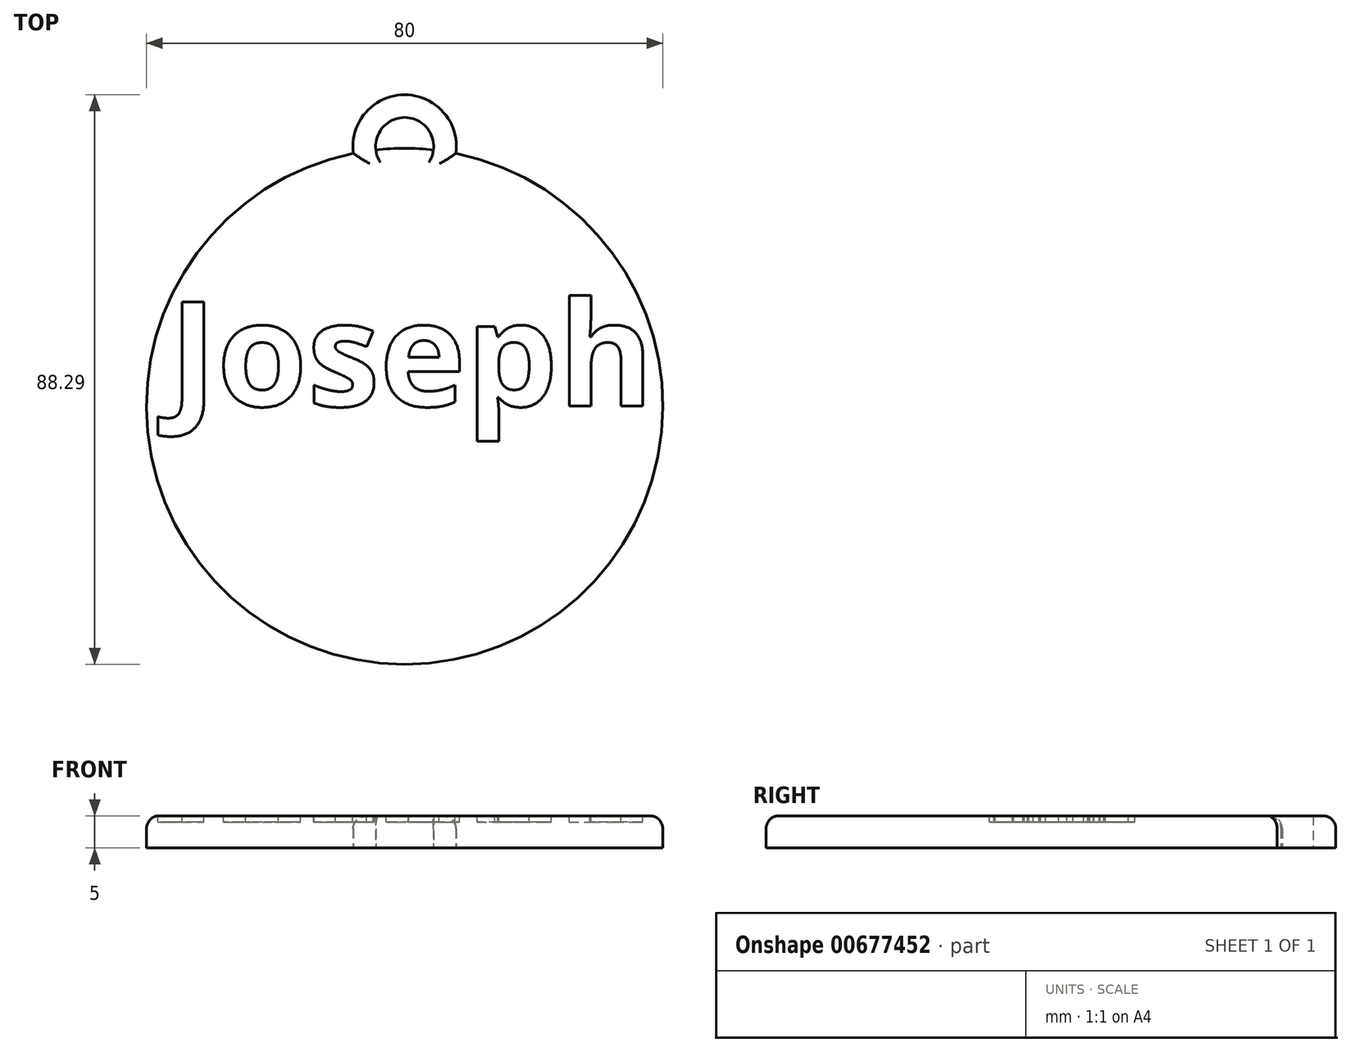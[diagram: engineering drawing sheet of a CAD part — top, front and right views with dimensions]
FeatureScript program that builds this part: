
annotation { "Feature Type Name" : "Feature", "Feature Type Description" : "" }
export const myFeature = defineFeature(function(context is Context, id is Id, definition is map)
    precondition{}
    {
        {
            var Q0;
            Q0=qCreatedBy(makeId("Top.planeOp"),FACE);
            var sketch = newSketch(context, id + "F0", { "sketchPlane" : qUnion([Q0])});
            skCircle(sketch, "E0", {"center": v(0, 0) * mm, "radius": 40 * mm});
            skSolve(sketch);
        }
        {
            var Q0;
            Q0 = qSketchRegion(id + "F0", true);
            var Q1;
            Q1 = qSketchRegion(id + "F4", true);
            extrude(context, id + "F1", {"entities" : qUnion([Q0, Q1]), "depth" : 5 * mm, "offsetDistance" : 25.4 * mm});
        }
        {
            var Q0;
            Q0=makeQuery(id+"F1.opExtrude","CAP_FACE",FACE,{"disambiguationData":[OSD([sQuery(id+"F0.wireOp",EDGE,"E0")])],"isStart":false});
            var sketch = newSketch(context, id + "F2", { "sketchPlane" : qUnion([Q0])});
            skText(sketch, "E1", { "text": "Joseph", "fontName": "OpenSans-Bold.ttf"});
            const initialGuessF2  = {"E1": [-0.03654, 3e-05, 1, 0, 0.01625]};
            skSetInitialGuess(sketch, initialGuessF2);
            skSolve(sketch);
        }
        {
            var Q0;
            Q0 = qSketchRegion(id + "F2", true);
            extrude(context, id + "F3", {"entities" : qUnion([Q0]), "operationType" : NewBodyOperationType.REMOVE, "oppositeDirection" : true, "depth" : 1 * mm, "offsetDistance" : 25.4 * mm});
        }
        {
            var Q0;
            Q0=qCreatedBy(makeId("Top.planeOp"),FACE);
            var sketch = newSketch(context, id + "F4", { "sketchPlane" : qUnion([Q0])});
            skCircle(sketch, "E2", {"center": v(0, 40.27) * mm, "radius": 4.5 * mm});
            skCircle(sketch, "E3", {"center": v(0, 40.27) * mm, "radius": 8.01 * mm});
            skSolve(sketch);
        }
        {
            var Q0;
            Q0=makeQuery(id+"F4.imprint","IMPRINT",FACE,{"disambiguationData":[TD([[makeQuery(id+"F4.imprint","IMPRINT",EDGE,{"derivedFrom":sQuery(id+"F4.wireOp",EDGE,"E2")}),-1.0]])]});
            extrude(context, id + "F5", {"entities" : qUnion([Q0]), "operationType" : NewBodyOperationType.ADD, "depth" : 5 * mm, "offsetDistance" : 25.4 * mm});
        }
        {
            var Q0;
            {var subQ0=sQuery(id+"F0.wireOp",EDGE,"E0");var subQ1=sQuery(id+"F4.wireOp",EDGE,"E3");Q0=makeQuery(id+"F5.boolean.opBoolean","SPLIT",EDGE,{"disambiguationData":[TD([makeQuery(id+"F5.opExtrude","SWEPT_FACE",FACE,{"disambiguationData":[OSD([subQ1])]})])],"derivedFrom":makeQuery(id+"F1.opExtrude","CAP_EDGE",EDGE,{"disambiguationData":[OSD([subQ0])],"isStart":false})});}
            fillet(context, id + "F6", {"entities" : qUnion([Q0]), "radius" : 2 * mm, "tangentPropagation" : true, "allowEdgeOverflow" : false});
        }
        {
            var Q0;
            {var subQ0=sQuery(id+"F0.wireOp",EDGE,"E0");var subQ1=sQuery(id+"F4.wireOp",EDGE,"E2");Q0=makeQuery(id+"F5.boolean.opBoolean","SPLIT",EDGE,{"disambiguationData":[TD([makeQuery(id+"F5.opExtrude","SWEPT_FACE",FACE,{"disambiguationData":[OSD([subQ1])]})])],"derivedFrom":makeQuery(id+"F1.opExtrude","CAP_EDGE",EDGE,{"disambiguationData":[OSD([subQ0])],"isStart":false})});}
            fillet(context, id + "F7", {"entities" : qUnion([Q0]), "radius" : 2 * mm, "tangentPropagation" : true, "allowEdgeOverflow" : false});
        }
        {
            var Q0;
            Q0=makeQuery(id+"F5.opExtrude","CAP_EDGE",EDGE,{"disambiguationData":[OSD([sQuery(id+"F4.wireOp",EDGE,"E3")])],"isStart":false});
            fillet(context, id + "F8", {"entities" : qUnion([Q0]), "radius" : 2 * mm, "tangentPropagation" : true, "allowEdgeOverflow" : false});
        }
    });
